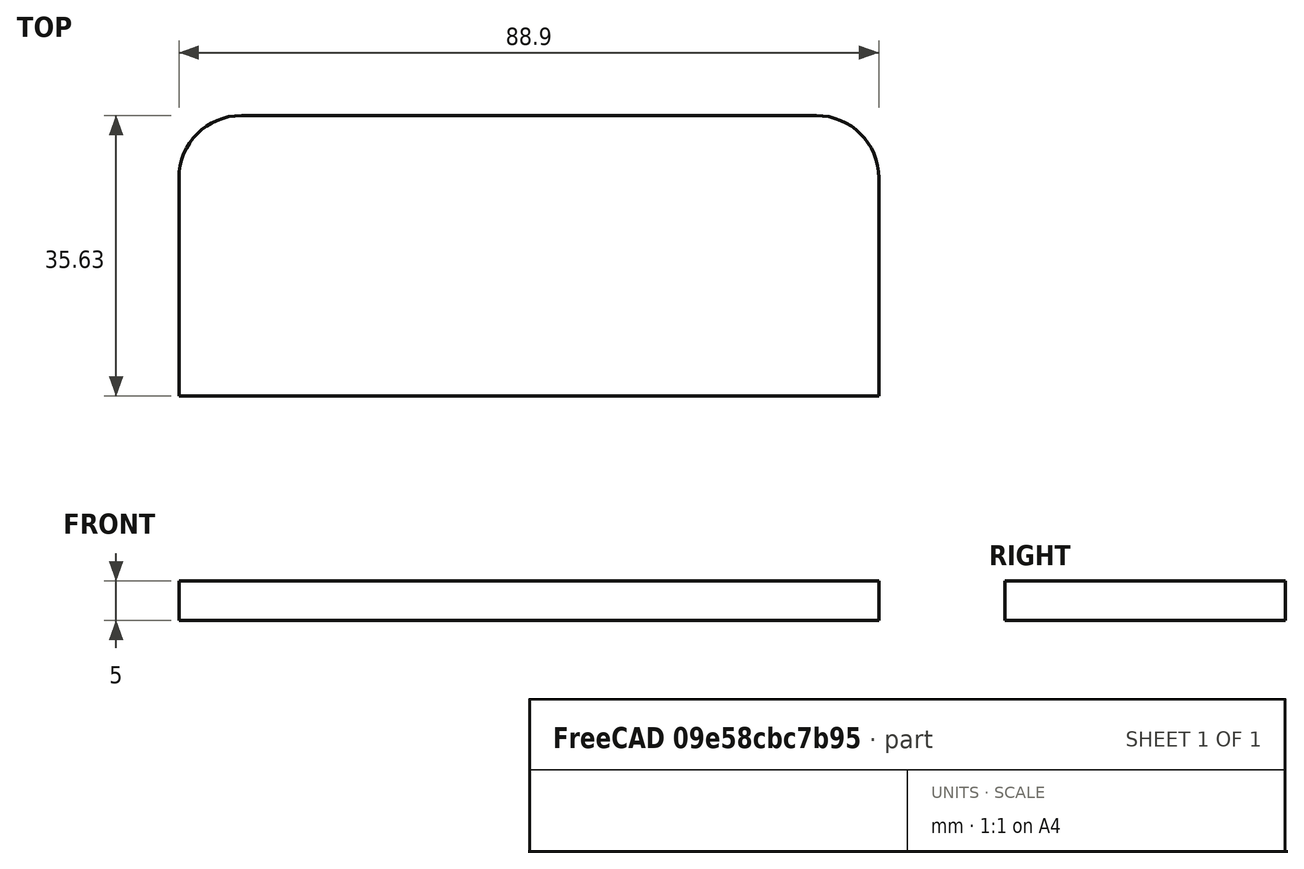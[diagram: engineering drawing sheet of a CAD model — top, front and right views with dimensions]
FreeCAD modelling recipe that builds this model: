
FCSTD DOCUMENT  (FreeCAD 0.20R29603 (Git))
Label: DoorHiingeRouterTemplate
License: All rights reserved
LicenseURL: http://en.wikipedia.org/wiki/All_rights_reserved
objects: Sketcher::SketchObject×1, PartDesign::Pad×1, PartDesign::Body×1, App::Part×1
note: 4 computed .brp shape members not serialized (recipe doc carries the construction recipe); baked Part::Feature solids carry a one-line shape summary decoded from their .brp

FEATURE [Sketcher::SketchObject] Sketch001
  FullyConstrained = false
  MapMode = 5
  Support = -> [XY_Plane001]
  sketch-geometry (7):
    g0: LineSegment StartX=-49.9549 StartY=11.7743 StartZ=0 EndX=-49.9549 EndY=-15.9224 EndZ=0
    g1: LineSegment StartX=-49.9549 StartY=-15.9224 StartZ=0 EndX=38.9451 EndY=-15.9224 EndZ=0
    g2: LineSegment StartX=38.9451 StartY=-15.9224 StartZ=0 EndX=38.9451 EndY=11.7743 EndZ=0
    g3: LineSegment StartX=31.0076 StartY=19.7118 StartZ=0 EndX=-42.0174 EndY=19.7118 EndZ=0
    g4: GeomPoint X=0 Y=0 Z=0
    g5: ArcOfCircle CenterX=-42.0174 CenterY=11.7743 CenterZ=0 NormalX=0 NormalY=0 NormalZ=1 AngleXU=0 Radius=7.9375 StartAngle=1.5708 EndAngle=3.14159
    g6: ArcOfCircle CenterX=31.0076 CenterY=11.7743 CenterZ=0 NormalX=0 NormalY=0 NormalZ=1 AngleXU=0 Radius=7.9375 StartAngle=1e-16 EndAngle=1.5708
  constraints (14):
    c: Coincident(g0,g1)
    c: Coincident(g1,g2)
    c: Horizontal(g1)
    c: Horizontal(g3)
    c: Vertical(g0)
    c: Vertical(g2)
    c: Coincident(g4,g-1)
    c: Tangent(g0,g5) = -1.5708
    c: Tangent(g3,g5) = -1.5708
    c: Tangent(g3,g6) = -1.5708
    c: Tangent(g2,g6) = -1.5708
    c: Equal(g5,g6)
    c: Diameter(g6) = 15.875
    c: DistanceX(g1,g1) = 88.9
FEATURE [PartDesign::Pad] Pad
  Direction = (0,0,1)
  Length = 5
  Length2 = 10
  Profile = -> Sketch001
  ReferenceAxis = -> Sketch001 [N_Axis]
  Type = 0
FEATURE [PartDesign::Body] Body
  Group = -> [Sketch001,Pad]
  Origin = -> Origin001
  Tip = -> Pad
FEATURE [App::Part] Part
  Group = -> [Body]
  Origin = -> Origin
